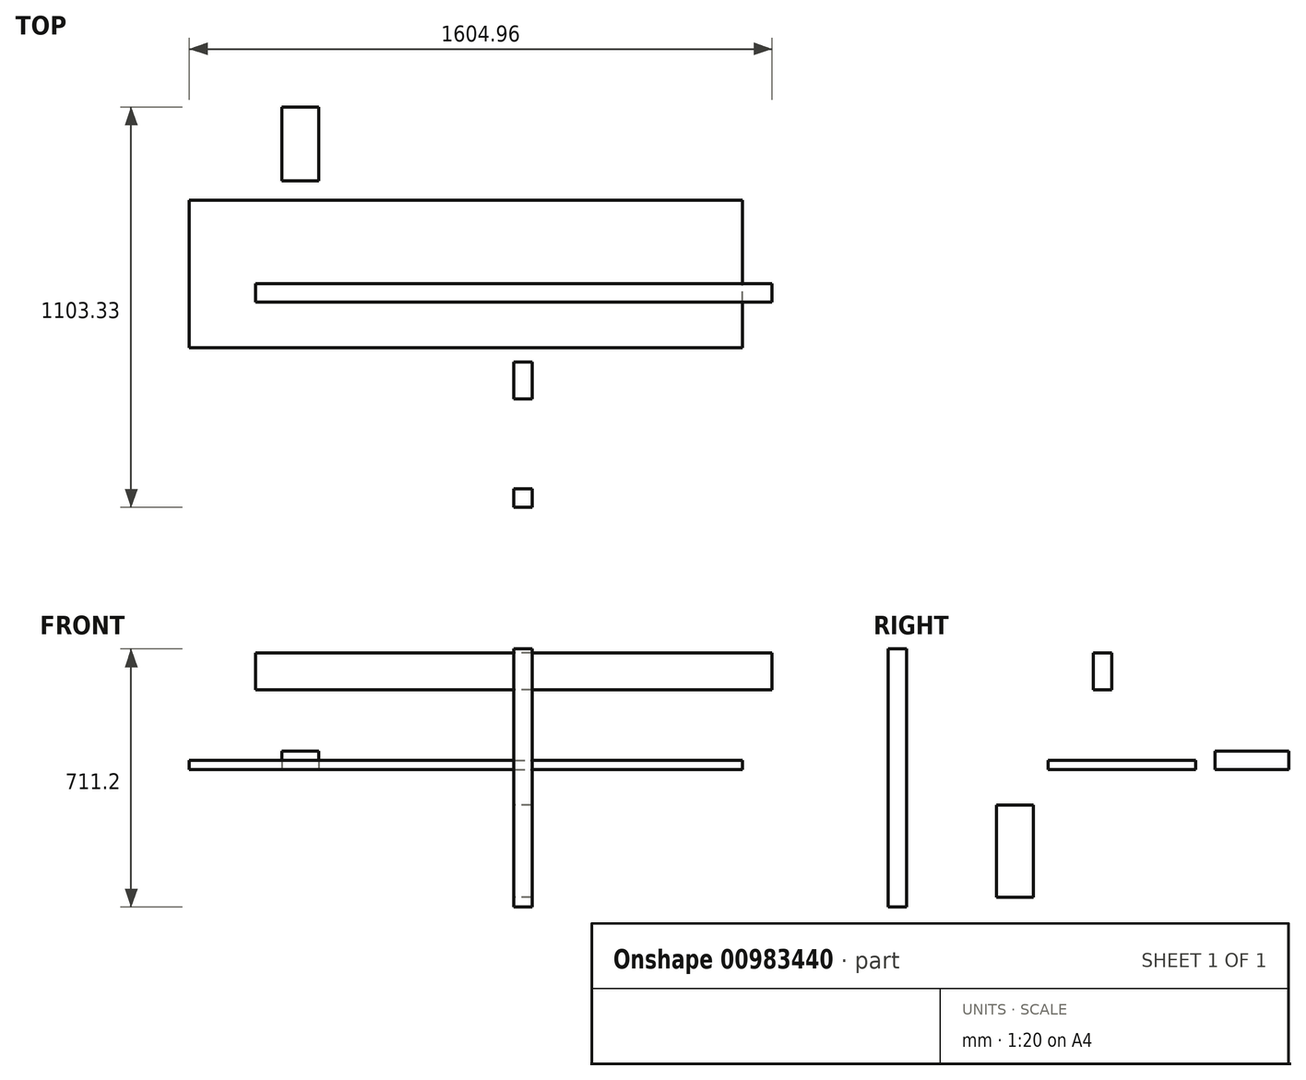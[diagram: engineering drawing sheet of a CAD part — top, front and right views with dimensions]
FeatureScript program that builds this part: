
annotation { "Feature Type Name" : "Feature", "Feature Type Description" : "" }
export const myFeature = defineFeature(function(context is Context, id is Id, definition is map)
    precondition{}
    {
        {
            var Q0;
            Q0=qCreatedBy(makeId("Top.planeOp"),FACE);
            var sketch = newSketch(context, id + "F0", { "sketchPlane" : qUnion([Q0])});
            skLineSegment(sketch, "E0.bottom", {"start": v(-893.76, -267.14) * mm, "end": v(630.24, -267.14) * mm});
            skLineSegment(sketch, "E0.top", {"start": v(-893.76, 139.26) * mm, "end": v(630.24, 139.26) * mm});
            skLineSegment(sketch, "E0.left", {"start": v(-893.76, -267.14) * mm, "end": v(-893.76, 139.26) * mm});
            skLineSegment(sketch, "E0.right", {"start": v(630.24, -267.14) * mm, "end": v(630.24, 139.26) * mm});
            skSolve(sketch);
        }
        {
            var Q0;
            Q0=makeQuery(id+"F0.imprint","IMPRINT",FACE,{"disambiguationData":[TD([[makeQuery(id+"F0.imprint","IMPRINT",EDGE,{"derivedFrom":sQuery(id+"F0.wireOp",EDGE,"E0.bottom")}),1.0]])]});
            extrude(context, id + "F1", {"entities" : qUnion([Q0]), "depth" : 25.4 * mm, "offsetDistance" : 25.4 * mm});
        }
        {
            var Q0;
            Q0=qCreatedBy(makeId("Top.planeOp"),FACE);
            var sketch = newSketch(context, id + "F2", { "sketchPlane" : qUnion([Q0])});
            skLineSegment(sketch, "E1.bottom", {"start": v(-639.54, 396.11) * mm, "end": v(-537.94, 396.11) * mm});
            skLineSegment(sketch, "E1.top", {"start": v(-639.54, 192.91) * mm, "end": v(-537.94, 192.91) * mm});
            skLineSegment(sketch, "E1.left", {"start": v(-639.54, 396.11) * mm, "end": v(-639.54, 192.91) * mm});
            skLineSegment(sketch, "E1.right", {"start": v(-537.94, 396.11) * mm, "end": v(-537.94, 192.91) * mm});
            skSolve(sketch);
        }
        {
            var Q0;
            Q0=makeQuery(id+"F2.imprint","IMPRINT",FACE,{"disambiguationData":[TD([[makeQuery(id+"F2.imprint","IMPRINT",EDGE,{"derivedFrom":sQuery(id+"F2.wireOp",EDGE,"E1.bottom")}),-1.0]])]});
            extrude(context, id + "F3", {"entities" : qUnion([Q0]), "depth" : 50.8 * mm, "offsetDistance" : 25.4 * mm});
        }
        {
            var Q0;
            Q0=qCreatedBy(makeId("Right.planeOp"),FACE);
            var sketch = newSketch(context, id + "F4", { "sketchPlane" : qUnion([Q0])});
            skLineSegment(sketch, "E2.bottom", {"start": v(-707.22, 332.45) * mm, "end": v(-656.42, 332.45) * mm});
            skLineSegment(sketch, "E2.top", {"start": v(-707.22, -378.75) * mm, "end": v(-656.42, -378.75) * mm});
            skLineSegment(sketch, "E2.left", {"start": v(-707.22, 332.45) * mm, "end": v(-707.22, -378.75) * mm});
            skLineSegment(sketch, "E2.right", {"start": v(-656.42, 332.45) * mm, "end": v(-656.42, -378.75) * mm});
            skLineSegment(sketch, "E3.bottom", {"start": v(-408.57, -97.3) * mm, "end": v(-306.97, -97.3) * mm});
            skLineSegment(sketch, "E3.top", {"start": v(-408.57, -351.3) * mm, "end": v(-306.97, -351.3) * mm});
            skLineSegment(sketch, "E3.left", {"start": v(-408.57, -97.3) * mm, "end": v(-408.57, -351.3) * mm});
            skLineSegment(sketch, "E3.right", {"start": v(-306.97, -97.3) * mm, "end": v(-306.97, -351.3) * mm});
            skSolve(sketch);
        }
        {
            var Q0;
            Q0=makeQuery(id+"F4.imprint","IMPRINT",FACE,{"disambiguationData":[TD([[makeQuery(id+"F4.imprint","IMPRINT",EDGE,{"derivedFrom":sQuery(id+"F4.wireOp",EDGE,"E2.bottom")}),-1.0]])]});
            var Q1;
            Q1=makeQuery(id+"F4.imprint","IMPRINT",FACE,{"disambiguationData":[TD([[makeQuery(id+"F4.imprint","IMPRINT",EDGE,{"derivedFrom":sQuery(id+"F4.wireOp",EDGE,"E3.bottom")}),-1.0]])]});
            extrude(context, id + "F5", {"entities" : qUnion([Q0, Q1]), "depth" : 50.8 * mm, "offsetDistance" : 25.4 * mm});
        }
        {
            var Q0;
            Q0=qCreatedBy(makeId("Right.planeOp"),FACE);
            var sketch = newSketch(context, id + "F6", { "sketchPlane" : qUnion([Q0])});
            skLineSegment(sketch, "E4.bottom", {"start": v(-142.2, 322.01) * mm, "end": v(-91.4, 322.01) * mm});
            skLineSegment(sketch, "E4.top", {"start": v(-142.2, 220.41) * mm, "end": v(-91.4, 220.41) * mm});
            skLineSegment(sketch, "E4.left", {"start": v(-142.2, 322.01) * mm, "end": v(-142.2, 220.41) * mm});
            skLineSegment(sketch, "E4.right", {"start": v(-91.4, 322.01) * mm, "end": v(-91.4, 220.41) * mm});
            skSolve(sketch);
        }
        {
            var Q0;
            Q0=makeQuery(id+"F6.imprint","IMPRINT",FACE,{"disambiguationData":[TD([[makeQuery(id+"F6.imprint","IMPRINT",EDGE,{"derivedFrom":sQuery(id+"F6.wireOp",EDGE,"E4.bottom")}),-1.0]])]});
            extrude(context, id + "F7", {"entities" : qUnion([Q0]), "endBound" : BoundingType.SYMMETRIC, "depth" : 1422.4 * mm, "offsetDistance" : 25.4 * mm});
        }
    });
